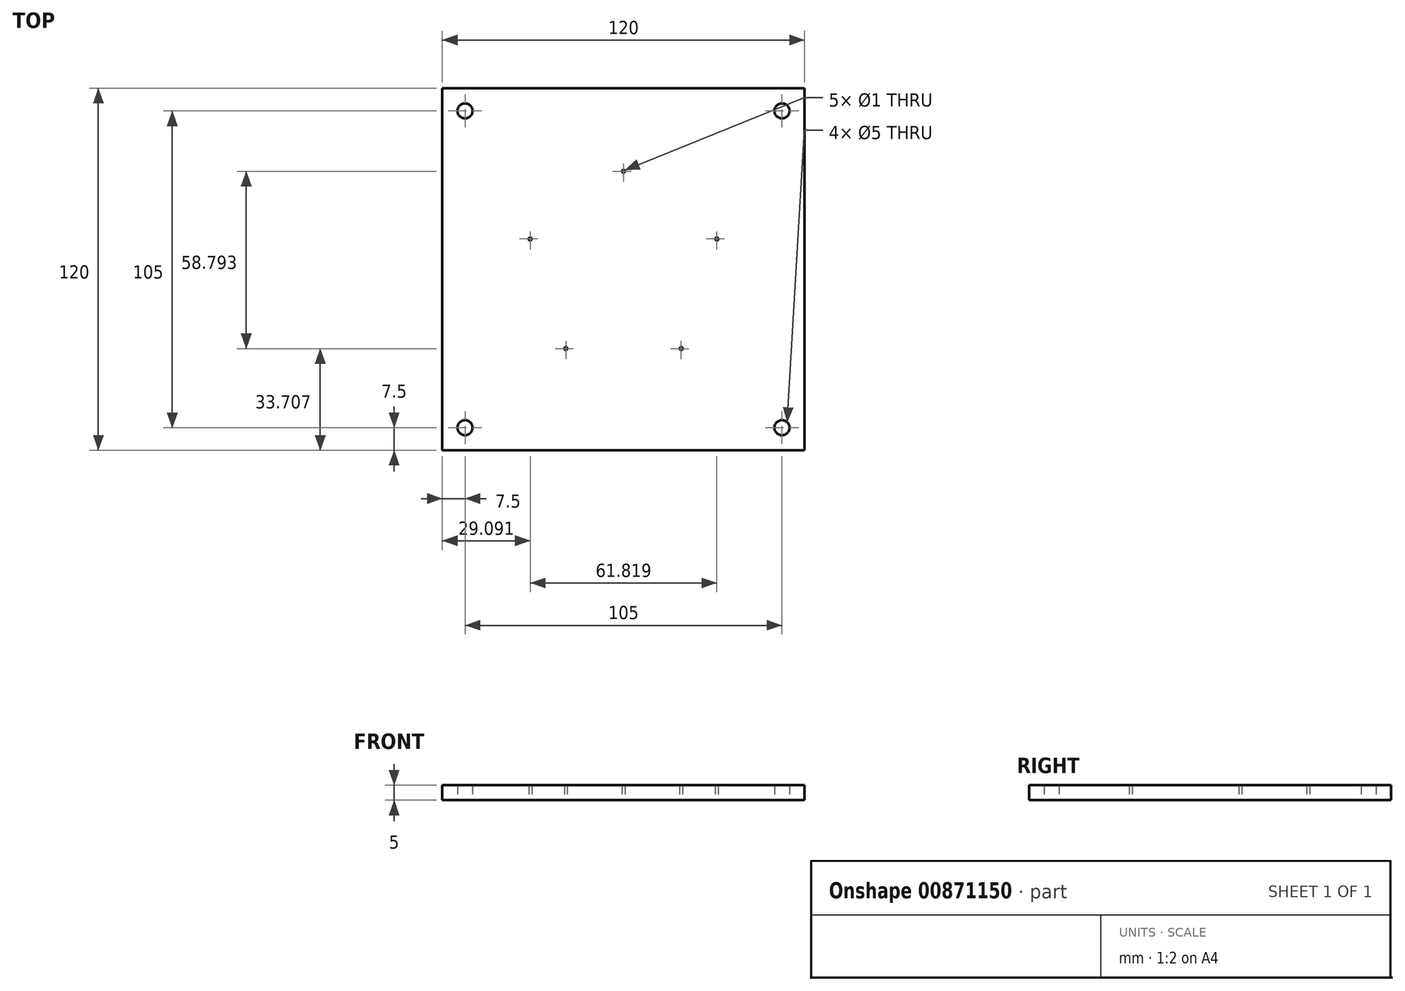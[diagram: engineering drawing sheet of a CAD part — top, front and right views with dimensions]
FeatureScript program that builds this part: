
annotation { "Feature Type Name" : "Feature", "Feature Type Description" : "" }
export const myFeature = defineFeature(function(context is Context, id is Id, definition is map)
    precondition{}
    {
        {
            var Q0;
            Q0=qCreatedBy(makeId("Top.planeOp"),FACE);
            var sketch = newSketch(context, id + "F0", { "sketchPlane" : qUnion([Q0])});
            skLineSegment(sketch, "E0.bottom", {"start": v(-60, 60) * mm, "end": v(60, 60) * mm});
            skLineSegment(sketch, "E0.top", {"start": v(-60, -60) * mm, "end": v(60, -60) * mm});
            skLineSegment(sketch, "E0.left", {"start": v(-60, 60) * mm, "end": v(-60, -60) * mm});
            skLineSegment(sketch, "E0.right", {"start": v(60, 60) * mm, "end": v(60, -60) * mm});
            skPoint(sketch, "E0.middle", {"position": v(0, 0) * mm});
            skLineSegment(sketch, "E1.bottom", {"start": v(52.5, 52.5) * mm, "end": v(-52.5, 52.5) * mm, "construction": true});
            skLineSegment(sketch, "E1.top", {"start": v(52.5, -52.5) * mm, "end": v(-52.5, -52.5) * mm, "construction": true});
            skLineSegment(sketch, "E1.left", {"start": v(52.5, 52.5) * mm, "end": v(52.5, -52.5) * mm, "construction": true});
            skLineSegment(sketch, "E1.right", {"start": v(-52.5, 52.5) * mm, "end": v(-52.5, -52.5) * mm, "construction": true});
            skCircle(sketch, "E2", {"center": v(-52.5, 52.5) * mm, "radius": 2.5 * mm});
            skCircle(sketch, "E3", {"center": v(52.5, 52.5) * mm, "radius": 2.5 * mm});
            skCircle(sketch, "E4", {"center": v(52.5, -52.5) * mm, "radius": 2.5 * mm});
            skCircle(sketch, "E5", {"center": v(-52.5, -52.5) * mm, "radius": 2.5 * mm});
            skCircle(sketch, "E6", {"center": v(0, 32.5) * mm, "radius": 16 * mm, "construction": true});
            skCircle(sketch, "E7", {"center": v(0, 0) * mm, "radius": 32.5 * mm, "construction": true});
            skCircle(sketch, "E8.1.0", {"center": v(-30.9, 10.04) * mm, "radius": 16 * mm, "construction": true});
            skCircle(sketch, "E8.2.0", {"center": v(-19.1, -26.3) * mm, "radius": 16 * mm, "construction": true});
            skCircle(sketch, "E8.3.0", {"center": v(19.1, -26.3) * mm, "radius": 16 * mm, "construction": true});
            skCircle(sketch, "E8.4.0", {"center": v(30.9, 10.04) * mm, "radius": 16 * mm, "construction": true});
            skCircle(sketch, "E9", {"center": v(0, 32.5) * mm, "radius": 0.5 * mm});
            skCircle(sketch, "E10.1.0", {"center": v(30.9, 10.04) * mm, "radius": 0.5 * mm});
            skCircle(sketch, "E10.2.0", {"center": v(19.1, -26.3) * mm, "radius": 0.5 * mm});
            skCircle(sketch, "E10.3.0", {"center": v(-19.1, -26.3) * mm, "radius": 0.5 * mm});
            skCircle(sketch, "E10.4.0", {"center": v(-30.9, 10.04) * mm, "radius": 0.5 * mm});
            skLineSegment(sketch, "E10.anchor1", {"start": v(0, 0) * mm, "end": v(0, 32.5) * mm, "construction": true});
            skLineSegment(sketch, "E10.anchor2", {"start": v(0, 0) * mm, "end": v(-30.9, 10.04) * mm, "construction": true});
            skSolve(sketch);
        }
        {
            var Q0;
            Q0=makeQuery(id+"F0.imprint","IMPRINT",FACE,{"disambiguationData":[TD([[makeQuery(id+"F0.imprint","IMPRINT",EDGE,{"derivedFrom":sQuery(id+"F0.wireOp",EDGE,"E0.bottom")}),-1.0]])]});
            extrude(context, id + "F1", {"entities" : qUnion([Q0]), "depth" : 5 * mm, "offsetDistance" : 25 * mm});
        }
    });
